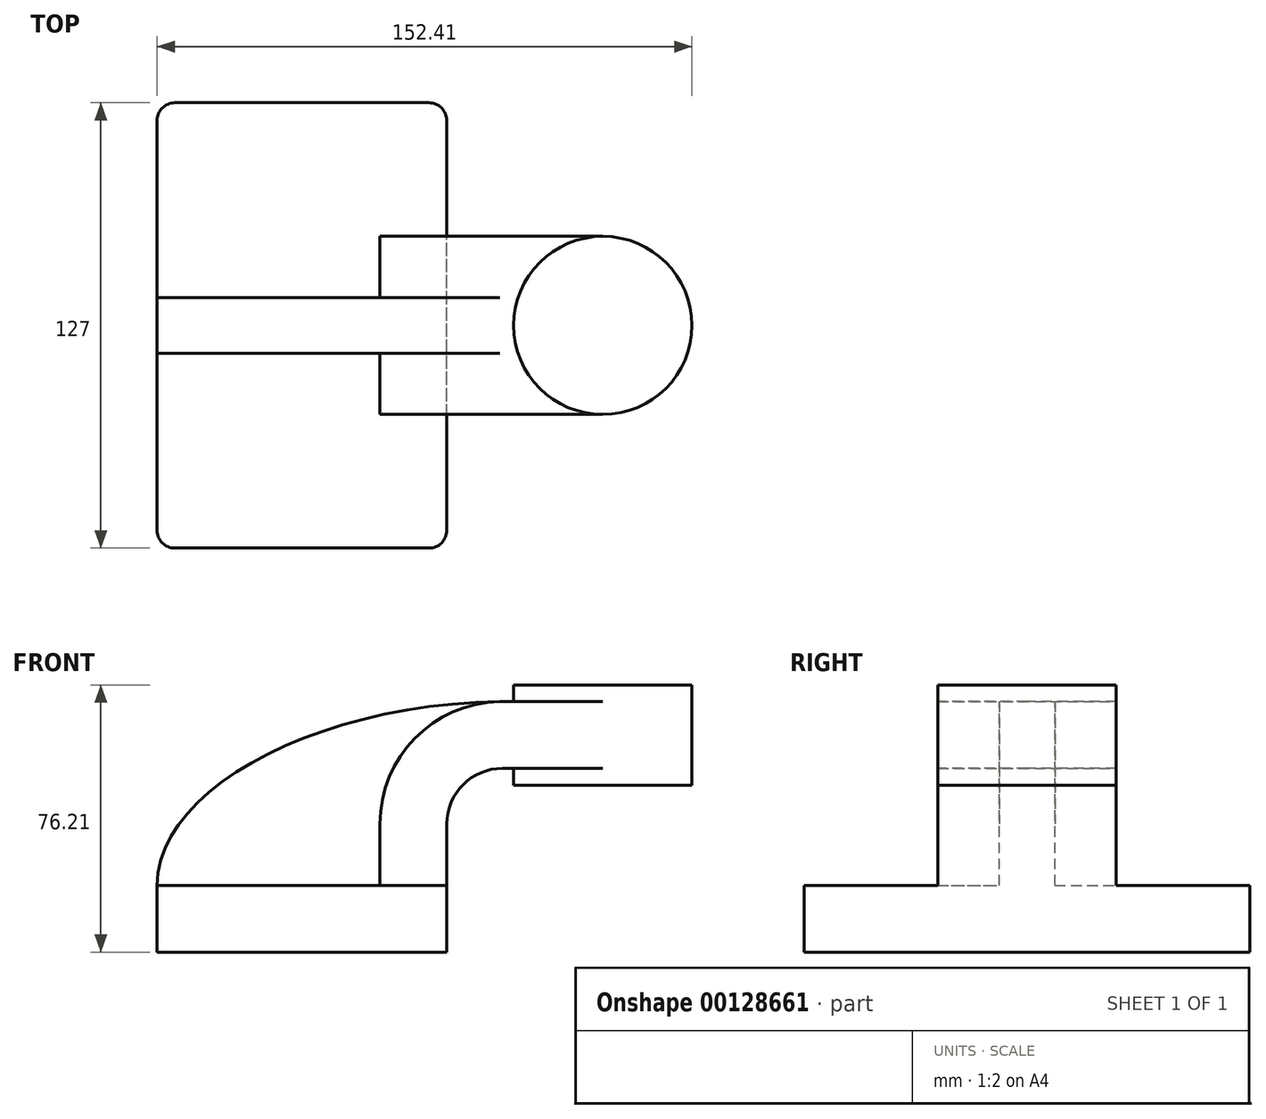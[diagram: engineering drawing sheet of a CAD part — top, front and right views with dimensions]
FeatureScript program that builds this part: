
annotation { "Feature Type Name" : "Feature", "Feature Type Description" : "" }
export const myFeature = defineFeature(function(context is Context, id is Id, definition is map)
    precondition{}
    {
        {
            var Q0;
            Q0=qCreatedBy(makeId("Front.planeOp"),FACE);
            var sketch = newSketch(context, id + "F0", { "sketchPlane" : qUnion([Q0])});
            skLineSegment(sketch, "E0.bottom", {"start": v(41.28, -9.52) * mm, "end": v(-41.28, -9.53) * mm});
            skLineSegment(sketch, "E0.top", {"start": v(41.28, 9.53) * mm, "end": v(-41.28, 9.53) * mm});
            skLineSegment(sketch, "E0.left", {"start": v(41.28, -9.52) * mm, "end": v(41.28, 9.53) * mm});
            skLineSegment(sketch, "E0.right", {"start": v(-41.28, -9.53) * mm, "end": v(-41.28, 9.53) * mm});
            skPoint(sketch, "E0.middle", {"position": v(0, 0) * mm});
            skLineSegment(sketch, "E1.bottom", {"start": v(111.12, 38.1) * mm, "end": v(60.33, 38.1) * mm});
            skLineSegment(sketch, "E1.top", {"start": v(111.12, 66.68) * mm, "end": v(60.33, 66.68) * mm});
            skLineSegment(sketch, "E1.left", {"start": v(111.12, 38.1) * mm, "end": v(111.12, 66.68) * mm});
            skLineSegment(sketch, "E1.right", {"start": v(60.33, 38.1) * mm, "end": v(60.33, 66.68) * mm});
            skPoint(sketch, "E1.middle", {"position": v(85.72, 52.39) * mm});
            skLineSegment(sketch, "E2", {"start": v(41.28, 9.53) * mm, "end": v(41.28, 27) * mm});
            skArc(sketch, "E3", {"start": v(41.27, 27) * mm, "mid": v(45.92, 38.23) * mm, "end": v(57.15, 42.88) * mm});
            skLineSegment(sketch, "E4", {"start": v(57.15, 42.88) * mm, "end": v(85.72, 42.88) * mm});
            skLineSegment(sketch, "E5.0", {"start": v(57.15, 61.93) * mm, "end": v(85.72, 61.93) * mm});
            skArc(sketch, "E5.1", {"start": v(22.23, 27) * mm, "mid": v(32.45, 51.7) * mm, "end": v(57.15, 61.93) * mm});
            skLineSegment(sketch, "E5.2", {"start": v(22.22, 9.53) * mm, "end": v(22.22, 27) * mm});
            skLineSegment(sketch, "E6", {"start": v(85.72, 38.1) * mm, "end": v(85.72, 66.68) * mm});
            skFitSpline(sketch, "E7", {"points": [v(-41.28, 9.52) * mm, v(57.15, 61.93) * mm], "startDerivative": vector(0.37, 82.66) * mm, "endDerivative": vector(157.91, 1.5) * mm});
            skSolve(sketch);
        }
        {
            var Q0;
            Q0=makeQuery(id+"F0.imprint","IMPRINT",FACE,{"disambiguationData":[TD([[makeQuery(id+"F0.imprint","IMPRINT",EDGE,{"derivedFrom":sQuery(id+"F0.wireOp",EDGE,"E0.bottom")}),-1.0]])]});
            extrude(context, id + "F1", {"entities" : qUnion([Q0]), "endBound" : BoundingType.SYMMETRIC, "depth" : 127 * mm});
        }
        {
            var Q0;
            {var subQ1=sQuery(id+"F0.wireOp",EDGE,"E2");Q0=makeQuery(id+"F0.imprint","IMPRINT",FACE,{"disambiguationData":[TD([[makeQuery(id+"F0.imprint","IMPRINT",EDGE,{"derivedFrom":subQ1}),1.0]])]});}
            var Q1;
            {var subQ0=sQuery(id+"F0.wireOp",EDGE,"E4");var subQ1=sQuery(id+"F0.wireOp",EDGE,"E1.right");var subQ2=makeQuery(id+"F0.imprint","INTERSECT",VERTEX,{"derivedFrom":[subQ1,subQ0]});Q1=makeQuery(id+"F0.imprint","IMPRINT",FACE,{"disambiguationData":[TD([[makeQuery(id+"F0.imprint","IMPRINT",EDGE,{"disambiguationData":[TD([[subQ2,-1.0]])],"derivedFrom":subQ1}),-1.0]])]});}
            extrude(context, id + "F2", {"entities" : qUnion([Q0, Q1]), "operationType" : NewBodyOperationType.ADD, "endBound" : BoundingType.SYMMETRIC, "depth" : 50.8 * mm});
        }
        {
            var Q0;
            {var subQ3=sQuery(id+"F0.wireOp",EDGE,"E5.2");Q0=makeQuery(id+"F0.imprint","IMPRINT",FACE,{"disambiguationData":[TD([[makeQuery(id+"F0.imprint","IMPRINT",EDGE,{"derivedFrom":subQ3}),1.0]])]});}
            extrude(context, id + "F3", {"entities" : qUnion([Q0]), "operationType" : NewBodyOperationType.ADD, "endBound" : BoundingType.SYMMETRIC, "depth" : 15.88 * mm});
        }
        {
            var Q0;
            Q0=makeQuery(id+"F1.opExtrude","CAP_EDGE",EDGE,{"disambiguationData":[OSD([sQuery(id+"F0.wireOp",EDGE,"E0.left")])],"isStart":false});
            var Q1;
            Q1=makeQuery(id+"F1.opExtrude","CAP_EDGE",EDGE,{"disambiguationData":[OSD([sQuery(id+"F0.wireOp",EDGE,"E0.right")])],"isStart":false});
            var Q2;
            Q2=makeQuery(id+"F1.opExtrude","CAP_EDGE",EDGE,{"disambiguationData":[OSD([sQuery(id+"F0.wireOp",EDGE,"E0.left")])],"isStart":true});
            var Q3;
            Q3=makeQuery(id+"F1.opExtrude","CAP_EDGE",EDGE,{"disambiguationData":[OSD([sQuery(id+"F0.wireOp",EDGE,"E0.right")])],"isStart":true});
            fillet(context, id + "F4", {"entities" : qUnion([Q0, Q1, Q2, Q3]), "radius" : 5.08 * mm, "tangentPropagation" : true, "allowEdgeOverflow" : false});
        }
        {
            var Q0;
            {var subQ0=sQuery(id+"F0.wireOp",EDGE,"E1.left");Q0=makeQuery(id+"F0.imprint","IMPRINT",FACE,{"disambiguationData":[TD([[makeQuery(id+"F0.imprint","IMPRINT",EDGE,{"derivedFrom":subQ0}),1.0]])]});}
            var Q1;
            Q1=sQuery(id+"F0.wireOp",EDGE,"E6");
            revolve(context, id + "F5", {"operationType" : NewBodyOperationType.ADD, "entities" : qUnion([Q0]), "axis" : qUnion([Q1]), "revolveType" : RevolveType.FULL});
        }
    });
